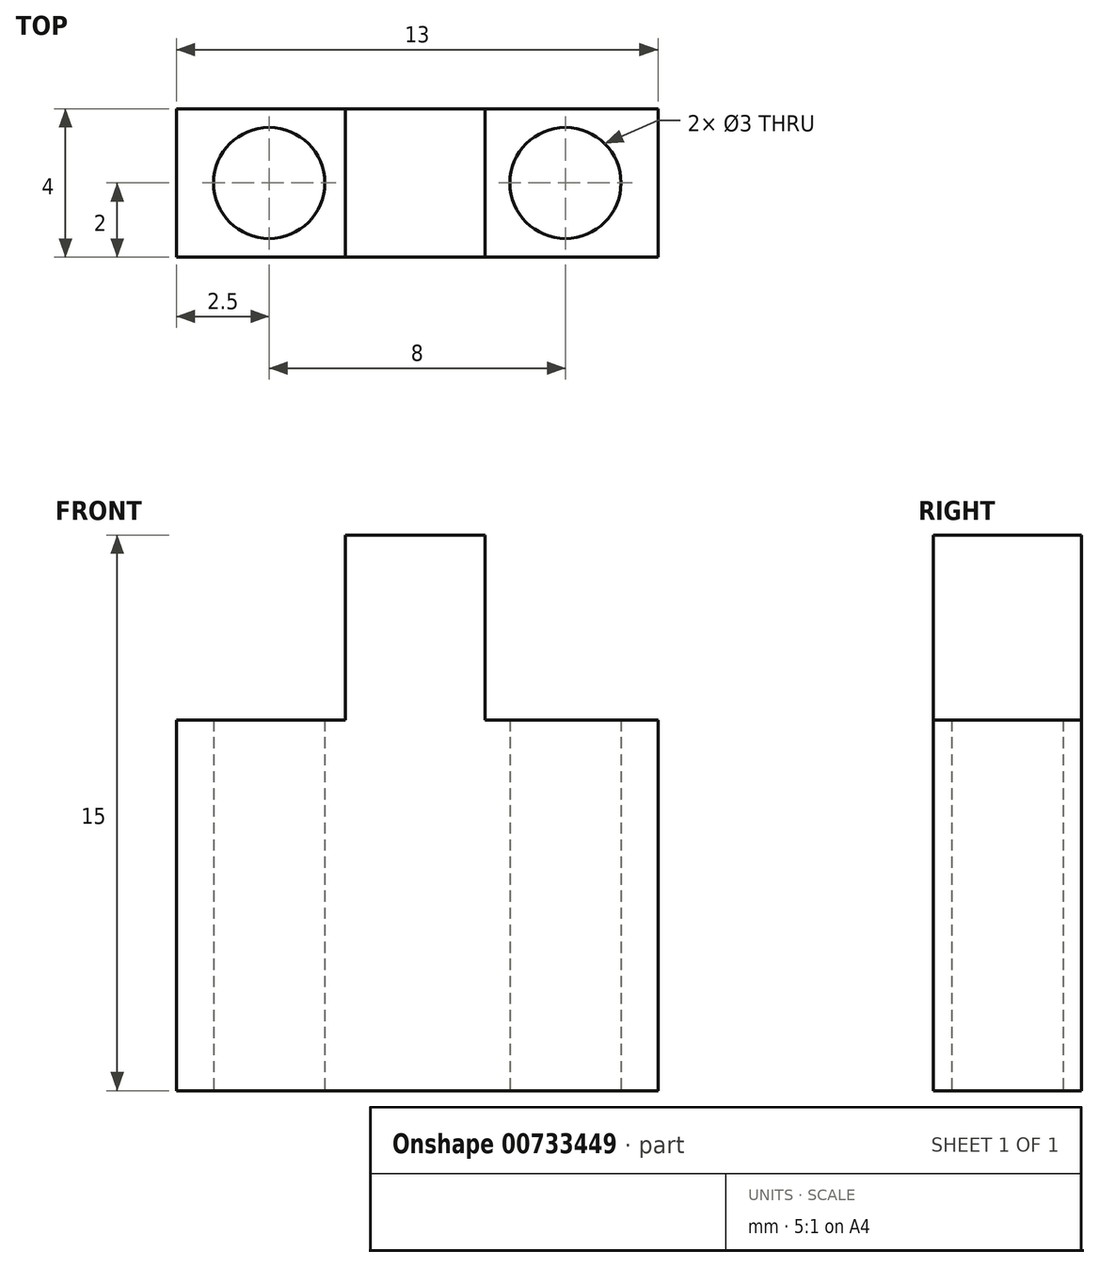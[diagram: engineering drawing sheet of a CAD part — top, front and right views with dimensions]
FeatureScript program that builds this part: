
annotation { "Feature Type Name" : "Feature", "Feature Type Description" : "" }
export const myFeature = defineFeature(function(context is Context, id is Id, definition is map)
    precondition{}
    {
        {
            var Q0;
            Q0=qCreatedBy(makeId("Top.planeOp"),FACE);
            var sketch = newSketch(context, id + "F0", { "sketchPlane" : qUnion([Q0])});
            skLineSegment(sketch, "E0.bottom", {"start": v(0, 0) * mm, "end": v(13, 0) * mm});
            skLineSegment(sketch, "E0.top", {"start": v(0, 4) * mm, "end": v(13, 4) * mm});
            skLineSegment(sketch, "E0.left", {"start": v(0, 0) * mm, "end": v(0, 4) * mm});
            skLineSegment(sketch, "E0.right", {"start": v(13, 0) * mm, "end": v(13, 4) * mm});
            skLineSegment(sketch, "E1", {"start": v(0, 2) * mm, "end": v(13, 2) * mm, "construction": true});
            skLineSegment(sketch, "E2", {"start": v(6.5, 4) * mm, "end": v(6.5, 0) * mm, "construction": true});
            skCircle(sketch, "E3", {"center": v(2.5, 2) * mm, "radius": 1.5 * mm});
            skCircle(sketch, "E4.MirrorC", {"center": v(10.5, 2) * mm, "radius": 1.5 * mm});
            skSolve(sketch);
        }
        {
            var Q0;
            Q0 = qSketchRegion(id + "F0", true);
            extrude(context, id + "F1", {"entities" : qUnion([Q0]), "depth" : 10 * mm, "offsetDistance" : 25 * mm});
        }
        {
            var Q0;
            Q0=makeQuery(id+"F1.opExtrude","CAP_FACE",FACE,{"disambiguationData":[OSD([sQuery(id+"F0.wireOp",EDGE,"E0.bottom"),sQuery(id+"F0.wireOp",EDGE,"E0.top"),sQuery(id+"F0.wireOp",EDGE,"E0.left"),sQuery(id+"F0.wireOp",EDGE,"E0.right"),sQuery(id+"F0.wireOp",EDGE,"E3"),sQuery(id+"F0.wireOp",EDGE,"E4.MirrorC")])],"isStart":false});
            var sketch = newSketch(context, id + "F2", { "sketchPlane" : qUnion([Q0])});
            skLineSegment(sketch, "E5.bottom", {"start": v(4.56, 4) * mm, "end": v(8.33, 4) * mm});
            skLineSegment(sketch, "E5.top", {"start": v(4.56, 0) * mm, "end": v(8.33, 0) * mm});
            skLineSegment(sketch, "E5.left", {"start": v(4.56, 4) * mm, "end": v(4.56, 0) * mm});
            skLineSegment(sketch, "E5.right", {"start": v(8.33, 4) * mm, "end": v(8.33, 0) * mm});
            skSolve(sketch);
        }
        {
            var Q0;
            Q0 = qSketchRegion(id + "F2", true);
            extrude(context, id + "F3", {"entities" : qUnion([Q0]), "operationType" : NewBodyOperationType.ADD, "depth" : 5 * mm, "offsetDistance" : 25 * mm});
        }
    });
